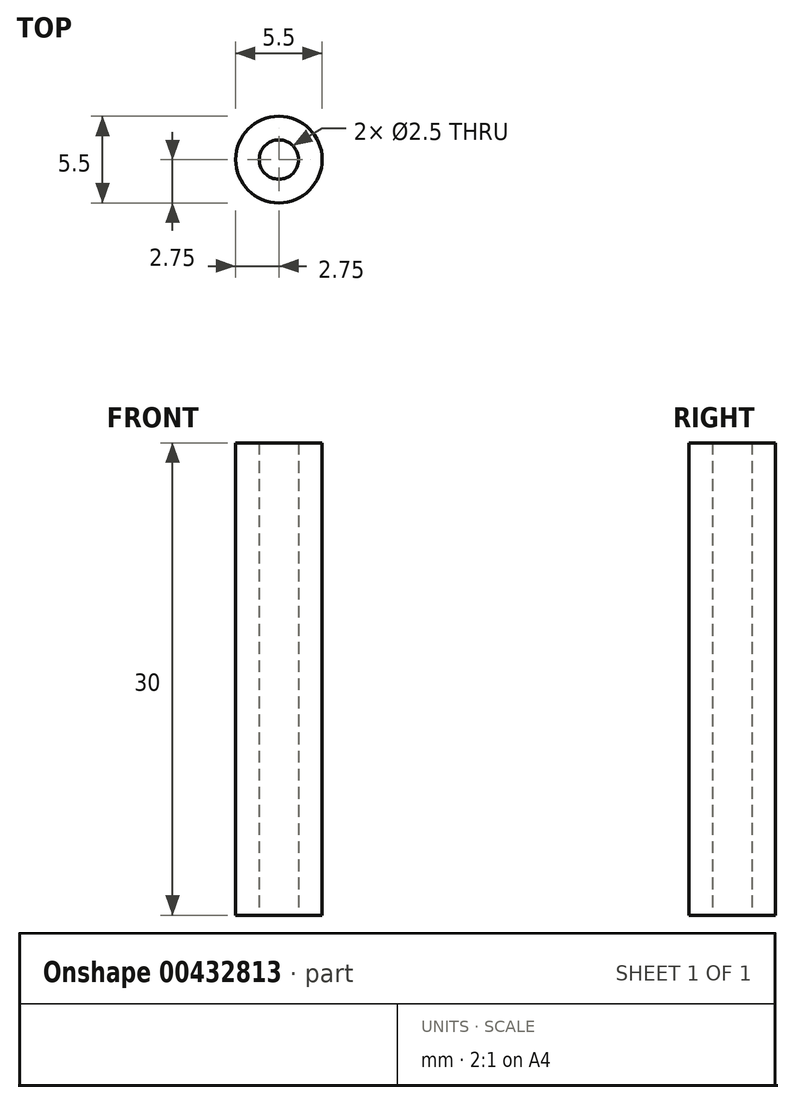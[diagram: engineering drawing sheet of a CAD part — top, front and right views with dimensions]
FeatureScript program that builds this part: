
annotation { "Feature Type Name" : "Feature", "Feature Type Description" : "" }
export const myFeature = defineFeature(function(context is Context, id is Id, definition is map)
    precondition{}
    {
        {
            var Q0;
            Q0=qCreatedBy(makeId("Top.planeOp"),FACE);
            var sketch = newSketch(context, id + "F0", { "sketchPlane" : qUnion([Q0])});
            skCircle(sketch, "E0", {"center": v(0, 0) * mm, "radius": 1.25 * mm});
            skCircle(sketch, "E1", {"center": v(0, 0) * mm, "radius": 2.75 * mm});
            skSolve(sketch);
        }
        {
            var Q0;
            Q0=makeQuery(id+"F0.imprint","IMPRINT",FACE,{"disambiguationData":[TD([[makeQuery(id+"F0.imprint","IMPRINT",EDGE,{"derivedFrom":sQuery(id+"F0.wireOp",EDGE,"E0")}),-1.0]])]});
            extrude(context, id + "F1", {"entities" : qUnion([Q0]), "depth" : 30 * mm});
        }
    });
